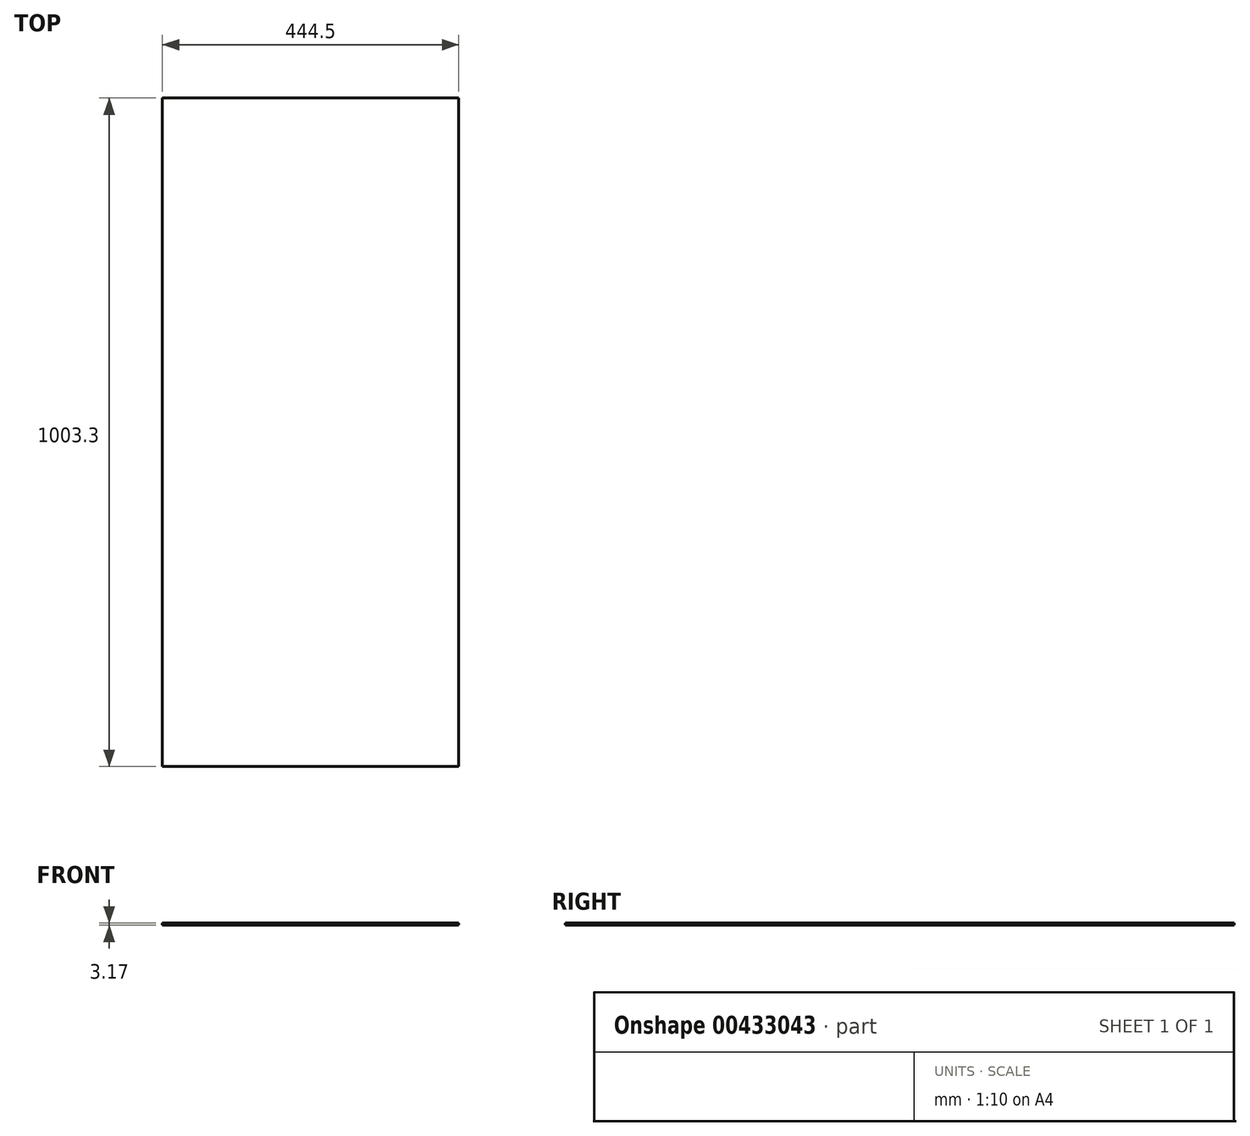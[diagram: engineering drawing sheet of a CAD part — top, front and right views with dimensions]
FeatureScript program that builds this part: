
annotation { "Feature Type Name" : "Feature", "Feature Type Description" : "" }
export const myFeature = defineFeature(function(context is Context, id is Id, definition is map)
    precondition{}
    {
        {
            var Q0;
            Q0=qCreatedBy(makeId("Top.planeOp"),FACE);
            var sketch = newSketch(context, id + "F0", { "sketchPlane" : qUnion([Q0])});
            skLineSegment(sketch, "E0.bottom", {"start": v(0, 0) * mm, "end": v(444.5, 0) * mm});
            skLineSegment(sketch, "E0.top", {"start": v(0, 1003.3) * mm, "end": v(444.5, 1003.3) * mm});
            skLineSegment(sketch, "E0.left", {"start": v(0, 0) * mm, "end": v(0, 1003.3) * mm});
            skLineSegment(sketch, "E0.right", {"start": v(444.5, 0) * mm, "end": v(444.5, 1003.3) * mm});
            skSolve(sketch);
        }
        {
            var Q0;
            Q0=makeQuery(id+"F0.imprint","IMPRINT",FACE,{"disambiguationData":[TD([[makeQuery(id+"F0.imprint","IMPRINT",EDGE,{"derivedFrom":sQuery(id+"F0.wireOp",EDGE,"E0.bottom")}),1.0]])]});
            extrude(context, id + "F1", {"entities" : qUnion([Q0]), "depth" : 3.17 * mm});
        }
    });
